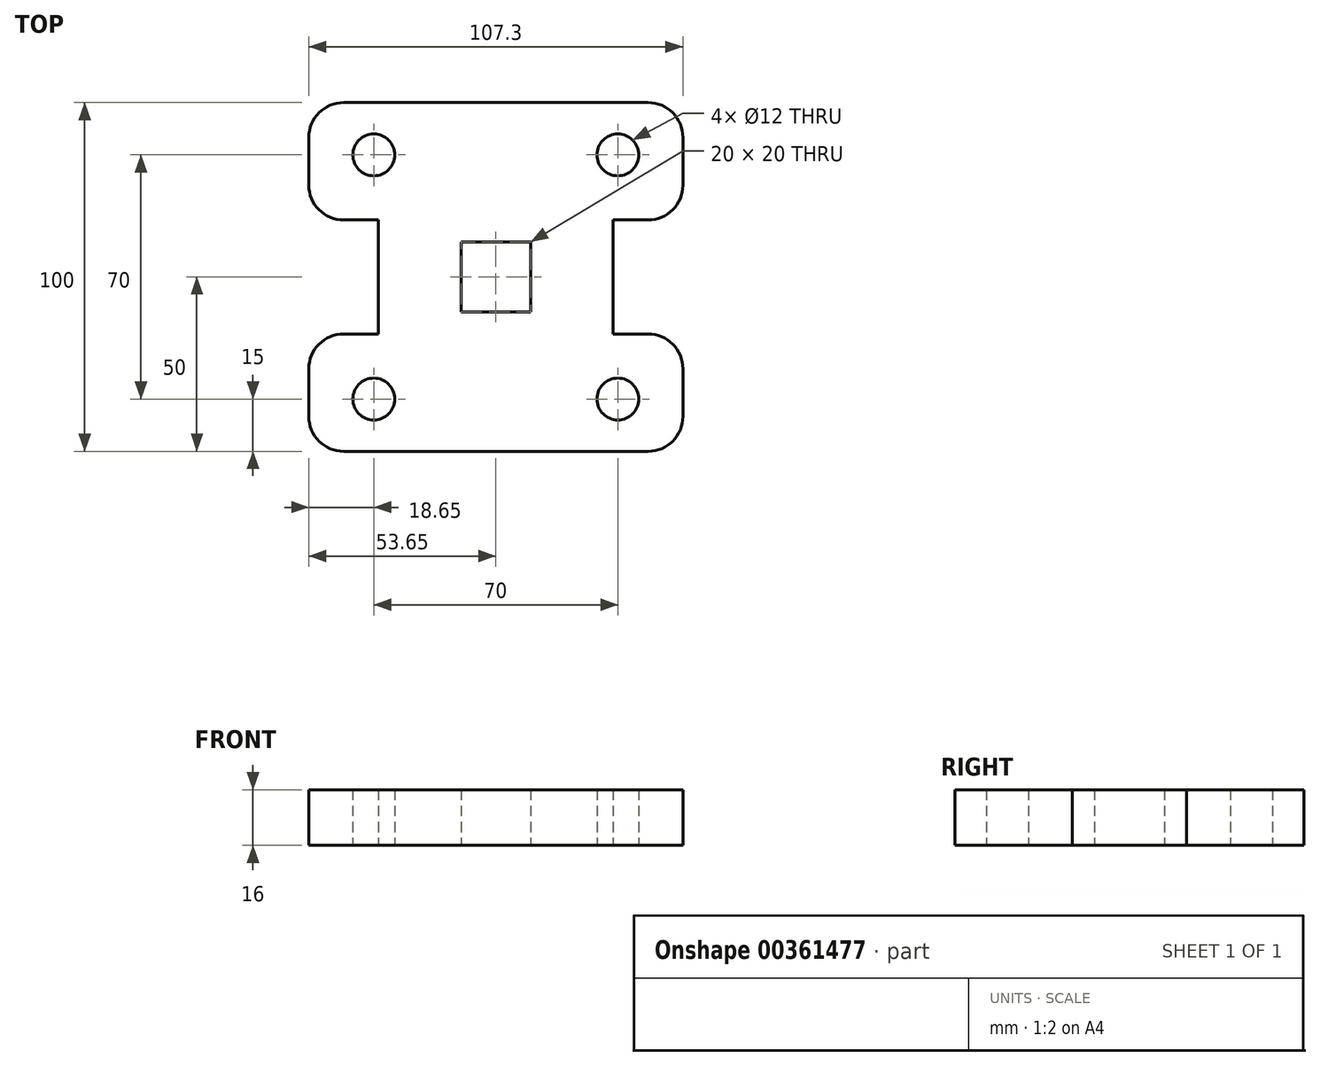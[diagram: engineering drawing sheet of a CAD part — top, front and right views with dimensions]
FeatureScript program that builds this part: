
annotation { "Feature Type Name" : "Feature", "Feature Type Description" : "" }
export const myFeature = defineFeature(function(context is Context, id is Id, definition is map)
    precondition{}
    {
        {
            var Q0;
            Q0=qCreatedBy(makeId("Top.planeOp"),FACE);
            var sketch = newSketch(context, id + "F0", { "sketchPlane" : qUnion([Q0])});
            skLineSegment(sketch, "E0", {"start": v(-33.65, -3.65) * mm, "end": v(-33.65, 16.35) * mm});
            skLineSegment(sketch, "E1", {"start": v(-33.65, 16.35) * mm, "end": v(-43.65, 16.35) * mm});
            skLineSegment(sketch, "E2", {"start": v(-53.65, 26.35) * mm, "end": v(-53.65, 40) * mm});
            skLineSegment(sketch, "E3", {"start": v(-43.65, 50) * mm, "end": v(0, 50) * mm});
            skCircle(sketch, "E4", {"center": v(-35, 35) * mm, "radius": 6 * mm});
            skLineSegment(sketch, "E5", {"start": v(-10, 0) * mm, "end": v(-10, 10) * mm});
            skLineSegment(sketch, "E6", {"start": v(-10, 10) * mm, "end": v(0, 10) * mm});
            skLineSegment(sketch, "E7.MirrorCS", {"start": v(43.65, 50) * mm, "end": v(0, 50) * mm});
            skLineSegment(sketch, "E8.MirrorCS", {"start": v(53.65, 26.35) * mm, "end": v(53.65, 40) * mm});
            skLineSegment(sketch, "E9.MirrorCS", {"start": v(33.65, 16.35) * mm, "end": v(43.65, 16.35) * mm});
            skLineSegment(sketch, "E10.MirrorCS", {"start": v(33.65, -3.65) * mm, "end": v(33.65, 16.35) * mm});
            skLineSegment(sketch, "E11.MirrorCS", {"start": v(10, 0) * mm, "end": v(10, 10) * mm});
            skLineSegment(sketch, "E12.MirrorCS", {"start": v(10, 10) * mm, "end": v(0, 10) * mm});
            skCircle(sketch, "E13.MirrorC", {"center": v(35, 35) * mm, "radius": 6 * mm});
            skLineSegment(sketch, "E14.MirrorCS", {"start": v(10, -10) * mm, "end": v(0, -10) * mm});
            skLineSegment(sketch, "E15.MirrorCS", {"start": v(-10, -10) * mm, "end": v(0, -10) * mm});
            skLineSegment(sketch, "E16.MirrorCS", {"start": v(-10, 0) * mm, "end": v(-10, -10) * mm});
            skLineSegment(sketch, "E17.MirrorCS", {"start": v(-33.65, 3.65) * mm, "end": v(-33.65, -16.35) * mm});
            skLineSegment(sketch, "E18.MirrorCS", {"start": v(-33.65, -16.35) * mm, "end": v(-43.65, -16.35) * mm});
            skLineSegment(sketch, "E19.MirrorCS", {"start": v(-53.65, -26.35) * mm, "end": v(-53.65, -40) * mm});
            skLineSegment(sketch, "E20.MirrorCS", {"start": v(-43.65, -50) * mm, "end": v(0, -50) * mm});
            skLineSegment(sketch, "E21.MirrorCS", {"start": v(43.65, -50) * mm, "end": v(0, -50) * mm});
            skLineSegment(sketch, "E22.MirrorCS", {"start": v(53.65, -26.35) * mm, "end": v(53.65, -40) * mm});
            skLineSegment(sketch, "E23.MirrorCS", {"start": v(33.65, -16.35) * mm, "end": v(43.65, -16.35) * mm});
            skLineSegment(sketch, "E24.MirrorCS", {"start": v(33.65, 3.65) * mm, "end": v(33.65, -16.35) * mm});
            skLineSegment(sketch, "E25.MirrorCS", {"start": v(10, 0) * mm, "end": v(10, -10) * mm});
            skCircle(sketch, "E26.MirrorC", {"center": v(35, -35) * mm, "radius": 6 * mm});
            skCircle(sketch, "E27.MirrorC", {"center": v(-35, -35) * mm, "radius": 6 * mm});
            skPoint(sketch, "E28.visualSharp", {"position": v(-53.65, 50) * mm});
            skArc(sketch, "E28.filletArc", {"start": v(-43.65, 50) * mm, "mid": v(-50.72, 47.07) * mm, "end": v(-53.65, 40) * mm});
            skPoint(sketch, "E29.visualSharp", {"position": v(53.65, 50) * mm});
            skArc(sketch, "E29.filletArc", {"start": v(53.65, 40) * mm, "mid": v(50.72, 47.07) * mm, "end": v(43.65, 50) * mm});
            skPoint(sketch, "E30.visualSharp", {"position": v(53.65, 16.35) * mm});
            skArc(sketch, "E30.filletArc", {"start": v(43.65, 16.35) * mm, "mid": v(50.72, 19.28) * mm, "end": v(53.65, 26.35) * mm});
            skPoint(sketch, "E31.visualSharp", {"position": v(53.65, -16.35) * mm});
            skArc(sketch, "E31.filletArc", {"start": v(53.65, -26.35) * mm, "mid": v(50.72, -19.28) * mm, "end": v(43.65, -16.35) * mm});
            skPoint(sketch, "E32.visualSharp", {"position": v(53.65, -50) * mm});
            skArc(sketch, "E32.filletArc", {"start": v(43.65, -50) * mm, "mid": v(50.72, -47.07) * mm, "end": v(53.65, -40) * mm});
            skPoint(sketch, "E33.visualSharp", {"position": v(-53.65, -50) * mm});
            skArc(sketch, "E33.filletArc", {"start": v(-53.65, -40) * mm, "mid": v(-50.72, -47.07) * mm, "end": v(-43.65, -50) * mm});
            skPoint(sketch, "E34.visualSharp", {"position": v(-53.65, -16.35) * mm});
            skArc(sketch, "E34.filletArc", {"start": v(-43.65, -16.35) * mm, "mid": v(-50.72, -19.28) * mm, "end": v(-53.65, -26.35) * mm});
            skPoint(sketch, "E35.visualSharp", {"position": v(-53.65, 16.35) * mm});
            skArc(sketch, "E35.filletArc", {"start": v(-53.65, 26.35) * mm, "mid": v(-50.72, 19.28) * mm, "end": v(-43.65, 16.35) * mm});
            skSolve(sketch);
        }
        {
            var Q0;
            Q0 = qSketchRegion(id + "F0", true);
            extrude(context, id + "F1", {"entities" : qUnion([Q0]), "depth" : 16 * mm});
        }
    });
